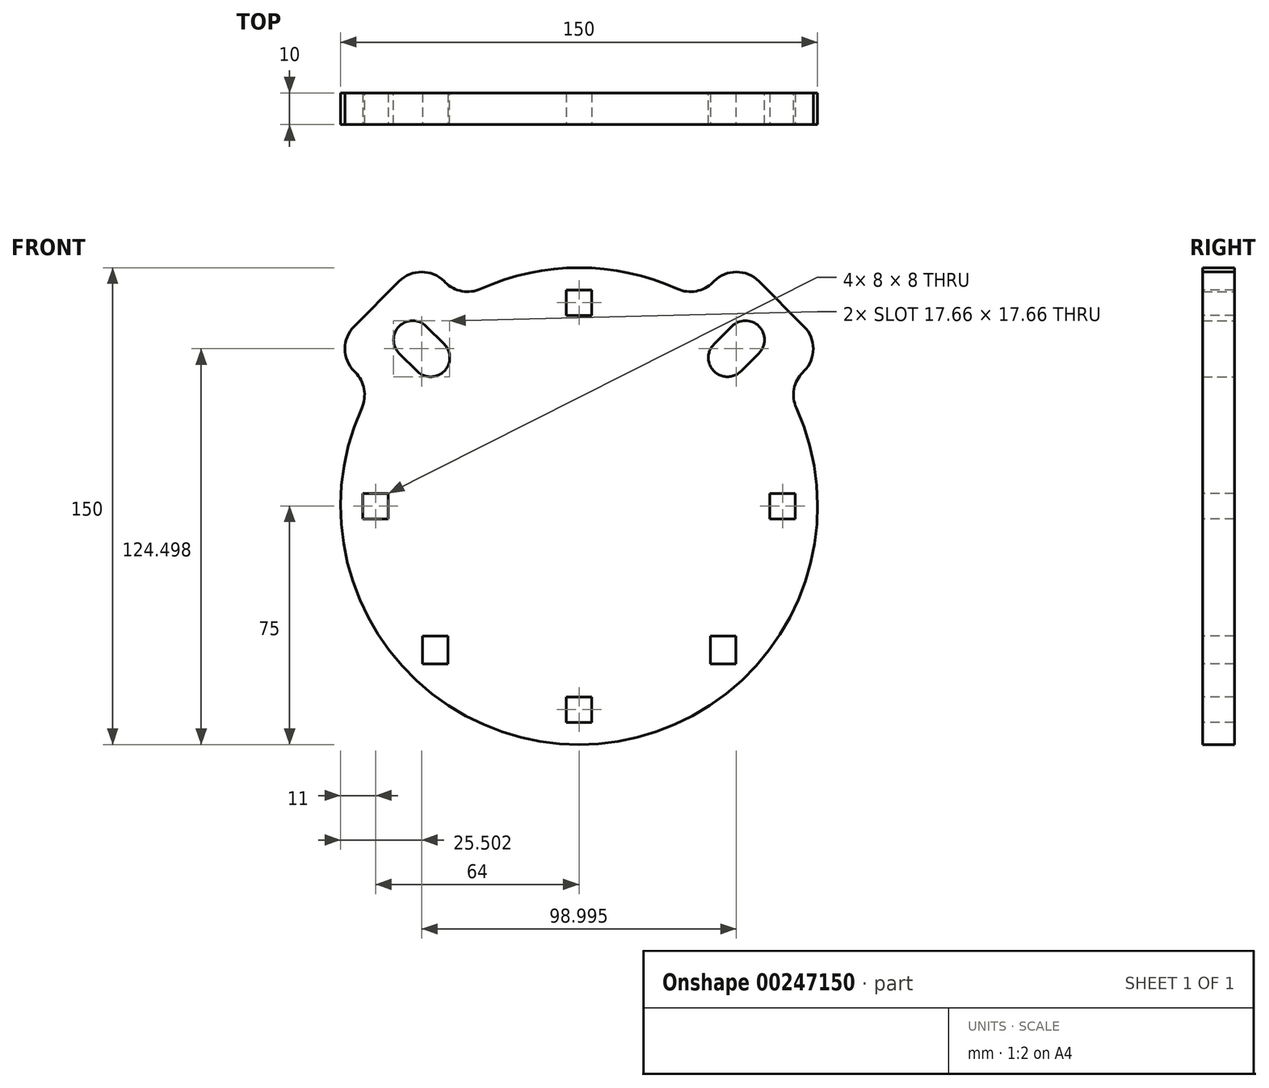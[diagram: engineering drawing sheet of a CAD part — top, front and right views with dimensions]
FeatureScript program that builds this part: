
annotation { "Feature Type Name" : "Feature", "Feature Type Description" : "" }
export const myFeature = defineFeature(function(context is Context, id is Id, definition is map)
    precondition{}
    {
        {
            var Q0;
            Q0=qCreatedBy(makeId("Front.planeOp"),FACE);
            var sketch = newSketch(context, id + "F0", { "sketchPlane" : qUnion([Q0])});
            skArc(sketch, "E0", {"start": v(-68.34, 30.9) * mm, "mid": v(0, -75) * mm, "end": v(68.34, 30.9) * mm});
            skLineSegment(sketch, "E1", {"start": v(0, 0) * mm, "end": v(0, 75) * mm, "construction": true});
            skLineSegment(sketch, "E2", {"start": v(0, 0) * mm, "end": v(-53.03, 53.03) * mm, "construction": true});
            skLineSegment(sketch, "E3", {"start": v(0, 0) * mm, "end": v(53.03, 53.03) * mm, "construction": true});
            skLineSegment(sketch, "E4", {"start": v(-70.38, 42.1) * mm, "end": v(-70.71, 42.43) * mm});
            skLineSegment(sketch, "E5", {"start": v(-70.71, 56.57) * mm, "end": v(-56.57, 70.71) * mm});
            skLineSegment(sketch, "E6", {"start": v(-42.43, 70.71) * mm, "end": v(-42.1, 70.38) * mm});
            skPoint(sketch, "E7.visualSharp", {"position": v(-77.78, 49.5) * mm});
            skArc(sketch, "E7.filletArc", {"start": v(-70.71, 56.57) * mm, "mid": v(-73.64, 49.5) * mm, "end": v(-70.71, 42.43) * mm});
            skPoint(sketch, "E8.visualSharp", {"position": v(-49.5, 77.78) * mm});
            skArc(sketch, "E8.filletArc", {"start": v(-42.43, 70.71) * mm, "mid": v(-49.5, 73.64) * mm, "end": v(-56.57, 70.71) * mm});
            skLineSegment(sketch, "E9.MirrorCS", {"start": v(70.38, 42.1) * mm, "end": v(70.71, 42.43) * mm});
            skArc(sketch, "E10.MirrorCS", {"start": v(70.71, 56.57) * mm, "mid": v(73.64, 49.5) * mm, "end": v(70.71, 42.43) * mm});
            skLineSegment(sketch, "E11.MirrorCS", {"start": v(42.43, 70.71) * mm, "end": v(42.1, 70.38) * mm});
            skLineSegment(sketch, "E12.MirrorCS", {"start": v(70.71, 56.57) * mm, "end": v(56.57, 70.71) * mm});
            skArc(sketch, "E13.MirrorCS", {"start": v(42.43, 70.71) * mm, "mid": v(49.5, 73.64) * mm, "end": v(56.57, 70.71) * mm});
            skArc(sketch, "E14.trimOffspring", {"start": v(30.9, 68.34) * mm, "mid": v(0, 75) * mm, "end": v(-30.9, 68.34) * mm});
            skPoint(sketch, "E15.visualSharp", {"position": v(36.97, 65.25) * mm});
            skArc(sketch, "E15.filletArc", {"start": v(30.9, 68.34) * mm, "mid": v(36.82, 67.61) * mm, "end": v(42.1, 70.38) * mm});
            skPoint(sketch, "E16.visualSharp", {"position": v(65.25, 36.97) * mm});
            skArc(sketch, "E16.filletArc", {"start": v(70.38, 42.1) * mm, "mid": v(67.61, 36.82) * mm, "end": v(68.34, 30.9) * mm});
            skPoint(sketch, "E17.visualSharp", {"position": v(-65.25, 36.97) * mm});
            skArc(sketch, "E17.filletArc", {"start": v(-68.34, 30.9) * mm, "mid": v(-67.61, 36.82) * mm, "end": v(-70.38, 42.1) * mm});
            skPoint(sketch, "E18.visualSharp", {"position": v(-36.97, 65.25) * mm});
            skArc(sketch, "E18.filletArc", {"start": v(-42.1, 70.38) * mm, "mid": v(-36.82, 67.61) * mm, "end": v(-30.9, 68.34) * mm});
            skSolve(sketch);
        }
        {
            var Q0;
            Q0=makeQuery(id+"F0.imprint","IMPRINT",FACE,{"disambiguationData":[TD([[makeQuery(id+"F0.imprint","IMPRINT",EDGE,{"derivedFrom":sQuery(id+"F0.wireOp",EDGE,"E0")}),1.0]])]});
            extrude(context, id + "F1", {"entities" : qUnion([Q0]), "offsetDistance" : 25 * mm, "depth" : 10 * mm});
        }
        {
            var Q0;
            Q0=makeQuery(id+"F1.opExtrude","CAP_FACE",FACE,{"disambiguationData":[OSD([sQuery(id+"F0.wireOp",EDGE,"E0"),sQuery(id+"F0.wireOp",EDGE,"E4"),sQuery(id+"F0.wireOp",EDGE,"E5"),sQuery(id+"F0.wireOp",EDGE,"E6"),sQuery(id+"F0.wireOp",EDGE,"E7.filletArc"),sQuery(id+"F0.wireOp",EDGE,"E8.filletArc"),sQuery(id+"F0.wireOp",EDGE,"E9.MirrorCS"),sQuery(id+"F0.wireOp",EDGE,"E10.MirrorCS"),sQuery(id+"F0.wireOp",EDGE,"E11.MirrorCS"),sQuery(id+"F0.wireOp",EDGE,"E12.MirrorCS"),sQuery(id+"F0.wireOp",EDGE,"E13.MirrorCS"),sQuery(id+"F0.wireOp",EDGE,"E14.trimOffspring"),sQuery(id+"F0.wireOp",EDGE,"E15.filletArc"),sQuery(id+"F0.wireOp",EDGE,"E16.filletArc"),sQuery(id+"F0.wireOp",EDGE,"E17.filletArc"),sQuery(id+"F0.wireOp",EDGE,"E18.filletArc")])],"isStart":true});
            var sketch = newSketch(context, id + "F2", { "sketchPlane" : qUnion([Q0])});
            skLineSegment(sketch, "E19", {"start": v(-63.64, 63.64) * mm, "end": v(0, 0) * mm, "construction": true});
            skLineSegment(sketch, "E20", {"start": v(0, 0) * mm, "end": v(0, 75) * mm, "construction": true});
            skPoint(sketch, "E21.startSnap0", {"position": v(-73.64, 49.5) * mm});
            skLineSegment(sketch, "E22", {"start": v(-42.43, 50.91) * mm, "end": v(-48.08, 56.57) * mm});
            skLineSegment(sketch, "E23", {"start": v(-56.57, 48.08) * mm, "end": v(-50.91, 42.43) * mm});
            skArc(sketch, "E24", {"start": v(-48.08, 56.57) * mm, "mid": v(-56.57, 56.57) * mm, "end": v(-56.57, 48.08) * mm});
            skArc(sketch, "E25", {"start": v(-50.91, 42.43) * mm, "mid": v(-42.43, 42.43) * mm, "end": v(-42.43, 50.91) * mm});
            skLineSegment(sketch, "E26", {"start": v(-48.08, 56.57) * mm, "end": v(-56.57, 48.08) * mm, "construction": true});
            skLineSegment(sketch, "E27", {"start": v(-42.43, 50.91) * mm, "end": v(-50.91, 42.43) * mm, "construction": true});
            skLineSegment(sketch, "E28.MirrorCS", {"start": v(56.57, 48.08) * mm, "end": v(50.91, 42.43) * mm});
            skLineSegment(sketch, "E29.MirrorCS", {"start": v(42.43, 50.91) * mm, "end": v(48.08, 56.57) * mm});
            skArc(sketch, "E30.MirrorCS", {"start": v(50.91, 42.43) * mm, "mid": v(42.43, 42.43) * mm, "end": v(42.43, 50.91) * mm});
            skArc(sketch, "E31.MirrorCS", {"start": v(48.08, 56.57) * mm, "mid": v(56.57, 56.57) * mm, "end": v(56.57, 48.08) * mm});
            skSolve(sketch);
        }
        {
            var Q0;
            Q0 = qSketchRegion(id + "F2", true);
            extrude(context, id + "F3", {"entities" : qUnion([Q0]), "operationType" : NewBodyOperationType.REMOVE, "endBound" : BoundingType.THROUGH_ALL, "oppositeDirection" : true, "depth" : 25 * mm, "offsetDistance" : 25 * mm});
        }
        {
            var Q0;
            Q0=makeQuery(id+"F1.opExtrude","CAP_FACE",FACE,{"disambiguationData":[OSD([sQuery(id+"F0.wireOp",EDGE,"E0"),sQuery(id+"F0.wireOp",EDGE,"E4"),sQuery(id+"F0.wireOp",EDGE,"E5"),sQuery(id+"F0.wireOp",EDGE,"E6"),sQuery(id+"F0.wireOp",EDGE,"E7.filletArc"),sQuery(id+"F0.wireOp",EDGE,"E8.filletArc"),sQuery(id+"F0.wireOp",EDGE,"E9.MirrorCS"),sQuery(id+"F0.wireOp",EDGE,"E10.MirrorCS"),sQuery(id+"F0.wireOp",EDGE,"E11.MirrorCS"),sQuery(id+"F0.wireOp",EDGE,"E12.MirrorCS"),sQuery(id+"F0.wireOp",EDGE,"E13.MirrorCS"),sQuery(id+"F0.wireOp",EDGE,"E14.trimOffspring"),sQuery(id+"F0.wireOp",EDGE,"E15.filletArc"),sQuery(id+"F0.wireOp",EDGE,"E16.filletArc"),sQuery(id+"F0.wireOp",EDGE,"E17.filletArc"),sQuery(id+"F0.wireOp",EDGE,"E18.filletArc")])],"isStart":false});
            var sketch = newSketch(context, id + "F4", { "sketchPlane" : qUnion([Q0])});
            skCircle(sketch, "E32", {"center": v(0, 0) * mm, "radius": 64 * mm, "construction": true});
            skLineSegment(sketch, "E33", {"start": v(0, 64) * mm, "end": v(0, -64) * mm, "construction": true});
            skLineSegment(sketch, "E34", {"start": v(64, 0) * mm, "end": v(-64, 0) * mm, "construction": true});
            skLineSegment(sketch, "E35.bottom", {"start": v(68, 4) * mm, "end": v(60, 4) * mm});
            skLineSegment(sketch, "E35.top", {"start": v(68, -4) * mm, "end": v(60, -4) * mm});
            skLineSegment(sketch, "E35.left", {"start": v(68, 4) * mm, "end": v(68, -4) * mm});
            skLineSegment(sketch, "E35.right", {"start": v(60, 4) * mm, "end": v(60, -4) * mm});
            skPoint(sketch, "E35.middle", {"position": v(64, 0) * mm});
            skLineSegment(sketch, "E36.bottom", {"start": v(4, 68) * mm, "end": v(-4, 68) * mm});
            skLineSegment(sketch, "E36.top", {"start": v(4, 60) * mm, "end": v(-4, 60) * mm});
            skLineSegment(sketch, "E36.left", {"start": v(4, 68) * mm, "end": v(4, 60) * mm});
            skLineSegment(sketch, "E36.right", {"start": v(-4, 68) * mm, "end": v(-4, 60) * mm});
            skPoint(sketch, "E36.middle", {"position": v(0, 64) * mm});
            skPoint(sketch, "E37.MirrorP", {"position": v(0, -64) * mm});
            skLineSegment(sketch, "E38.MirrorCS", {"start": v(4, -68) * mm, "end": v(4, -60) * mm});
            skLineSegment(sketch, "E39.MirrorCS", {"start": v(-4, -68) * mm, "end": v(-4, -60) * mm});
            skLineSegment(sketch, "E40.MirrorCS", {"start": v(4, -60) * mm, "end": v(-4, -60) * mm});
            skLineSegment(sketch, "E41.MirrorCS", {"start": v(4, -68) * mm, "end": v(-4, -68) * mm});
            skLineSegment(sketch, "E42.MirrorCS", {"start": v(-60, 4) * mm, "end": v(-60, -4) * mm});
            skLineSegment(sketch, "E43.MirrorCS", {"start": v(-68, 4) * mm, "end": v(-68, -4) * mm});
            skPoint(sketch, "E44.MirrorP", {"position": v(-64, 0) * mm});
            skLineSegment(sketch, "E45.MirrorCS", {"start": v(-68, -4) * mm, "end": v(-60, -4) * mm});
            skLineSegment(sketch, "E46.MirrorCS", {"start": v(-68, 4) * mm, "end": v(-60, 4) * mm});
            skLineSegment(sketch, "E47", {"start": v(45.25, -45.25) * mm, "end": v(0, 0) * mm, "construction": true});
            skLineSegment(sketch, "E48", {"start": v(0, 0) * mm, "end": v(45.25, 45.25) * mm, "construction": true});
            skLineSegment(sketch, "E49.bottom", {"start": v(49.25, -40.87) * mm, "end": v(41.25, -40.87) * mm});
            skLineSegment(sketch, "E49.top", {"start": v(49.25, -49.64) * mm, "end": v(41.25, -49.64) * mm});
            skLineSegment(sketch, "E49.left", {"start": v(49.25, -40.87) * mm, "end": v(49.25, -49.64) * mm});
            skLineSegment(sketch, "E49.right", {"start": v(41.25, -40.87) * mm, "end": v(41.25, -49.64) * mm});
            skPoint(sketch, "E49.middle", {"position": v(45.25, -45.25) * mm});
            skLineSegment(sketch, "E50.MirrorCS", {"start": v(-49.25, -49.64) * mm, "end": v(-41.25, -49.64) * mm});
            skLineSegment(sketch, "E51.MirrorCS", {"start": v(-41.25, -40.87) * mm, "end": v(-41.25, -49.64) * mm});
            skLineSegment(sketch, "E52.MirrorCS", {"start": v(-49.25, -40.87) * mm, "end": v(-49.25, -49.64) * mm});
            skLineSegment(sketch, "E53.MirrorCS", {"start": v(-49.25, -40.87) * mm, "end": v(-41.25, -40.87) * mm});
            skPoint(sketch, "E54.MirrorP", {"position": v(-45.25, -45.25) * mm});
            skSolve(sketch);
        }
        {
            var Q0;
            Q0 = qSketchRegion(id + "F4", true);
            extrude(context, id + "F5", {"entities" : qUnion([Q0]), "operationType" : NewBodyOperationType.REMOVE, "endBound" : BoundingType.THROUGH_ALL, "oppositeDirection" : true, "depth" : 25 * mm, "offsetDistance" : 25 * mm});
        }
    });
